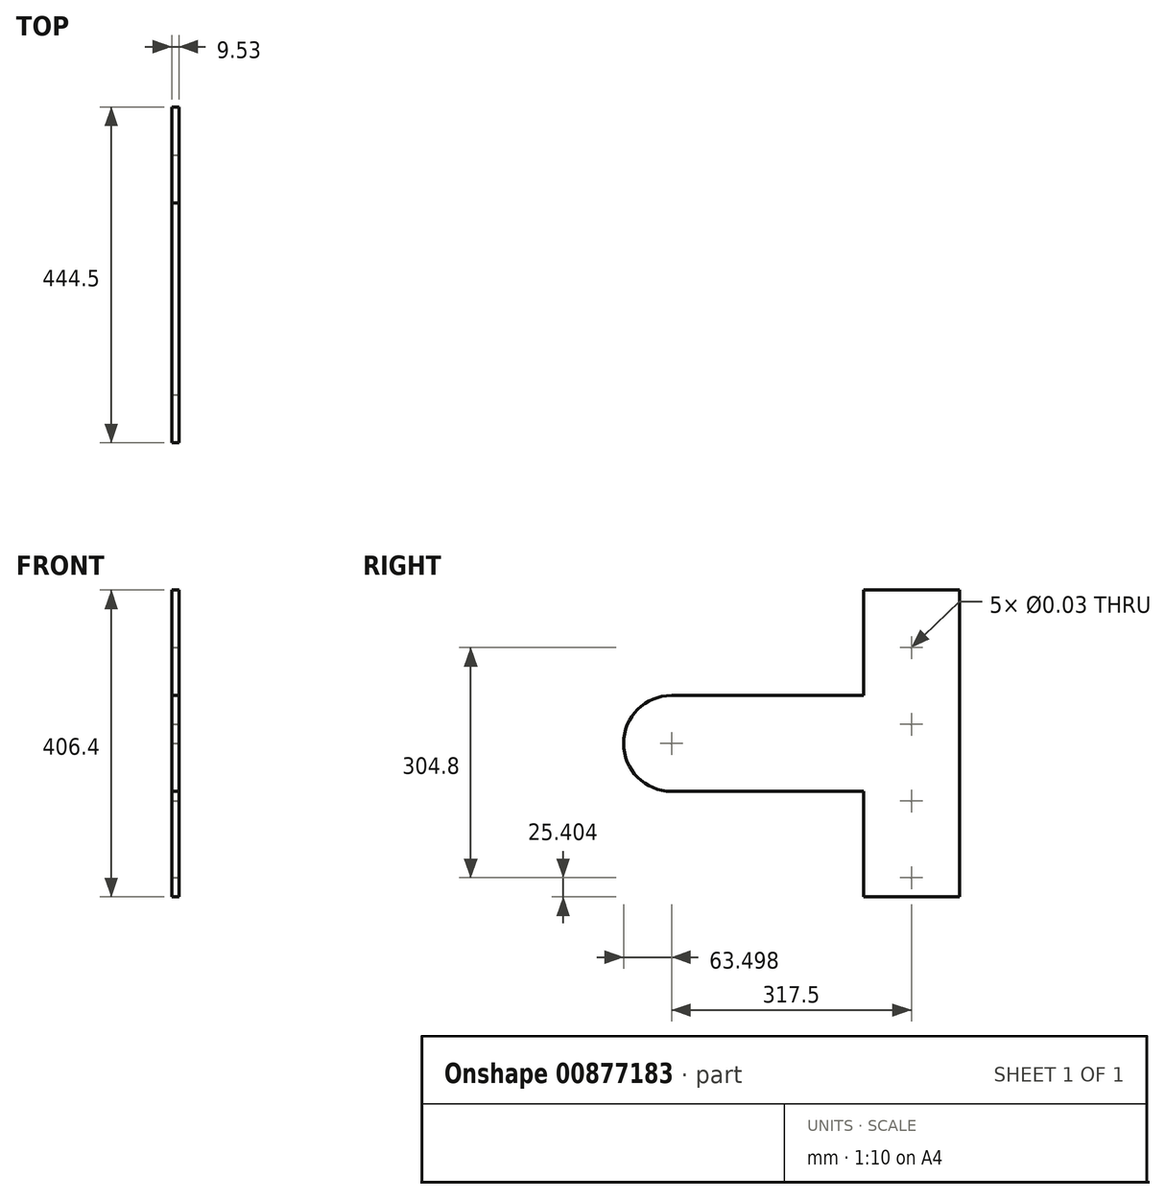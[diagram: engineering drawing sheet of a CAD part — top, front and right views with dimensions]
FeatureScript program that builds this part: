
annotation { "Feature Type Name" : "Feature", "Feature Type Description" : "" }
export const myFeature = defineFeature(function(context is Context, id is Id, definition is map)
    precondition{}
    {
        {
            var Q0;
            Q0=qCreatedBy(makeId("Right.planeOp"),FACE);
            var sketch = newSketch(context, id + "F0", { "sketchPlane" : qUnion([Q0])});
            skLineSegment(sketch, "E0.bottom", {"start": v(-37.3, -33.99) * mm, "end": v(89.7, -33.99) * mm});
            skLineSegment(sketch, "E0.top", {"start": v(-37.3, 372.41) * mm, "end": v(89.7, 372.41) * mm});
            skLineSegment(sketch, "E0.left", {"start": v(-37.3, -33.99) * mm, "end": v(-37.3, 372.41) * mm});
            skLineSegment(sketch, "E0.right", {"start": v(89.7, -33.99) * mm, "end": v(89.7, 372.41) * mm});
            skSolve(sketch);
        }
        {
            var Q0;
            Q0=makeQuery(id+"F0.imprint","IMPRINT",FACE,{"disambiguationData":[TD([[makeQuery(id+"F0.imprint","IMPRINT",EDGE,{"derivedFrom":sQuery(id+"F0.wireOp",EDGE,"E0.bottom")}),1.0]])]});
            extrude(context, id + "F1", {"entities" : qUnion([Q0]), "depth" : 9.52 * mm, "offsetDistance" : 25.4 * mm});
        }
        {
            var Q0;
            Q0=makeQuery(id+"F1.opExtrude","CAP_FACE",FACE,{"disambiguationData":[OSD([sQuery(id+"F0.wireOp",EDGE,"E0.bottom"),sQuery(id+"F0.wireOp",EDGE,"E0.top"),sQuery(id+"F0.wireOp",EDGE,"E0.left"),sQuery(id+"F0.wireOp",EDGE,"E0.right")])],"isStart":false});
            var sketch = newSketch(context, id + "F2", { "sketchPlane" : qUnion([Q0])});
            skLineSegment(sketch, "E1", {"start": v(-37.3, 169.21) * mm, "end": v(-37.3, 232.71) * mm});
            skLineSegment(sketch, "E2", {"start": v(-37.3, 232.71) * mm, "end": v(-354.8, 232.71) * mm});
            skLineSegment(sketch, "E3", {"start": v(-354.8, 232.71) * mm, "end": v(-354.8, 105.71) * mm});
            skLineSegment(sketch, "E4", {"start": v(-354.8, 105.71) * mm, "end": v(-37.3, 105.71) * mm});
            skLineSegment(sketch, "E5", {"start": v(-37.3, 105.71) * mm, "end": v(-37.3, 169.21) * mm});
            skSolve(sketch);
        }
        {
            var Q0;
            Q0=makeQuery(id+"F2.imprint","IMPRINT",FACE,{"disambiguationData":[TD([[makeQuery(id+"F2.imprint","IMPRINT",EDGE,{"derivedFrom":sQuery(id+"F2.wireOp",EDGE,"E1")}),1.0]])]});
            extrude(context, id + "F3", {"entities" : qUnion([Q0]), "operationType" : NewBodyOperationType.ADD, "oppositeDirection" : true, "depth" : 9.52 * mm, "offsetDistance" : 25.4 * mm});
        }
        {
            var Q0;
            Q0=makeQuery(id+"F3.opExtrude","SWEPT_EDGE",EDGE,{"disambiguationData":[OSD([sQuery(id+"F2.wireOp",EDGE,"E2"),sQuery(id+"F2.wireOp",EDGE,"E3")])]});
            var Q1;
            Q1=makeQuery(id+"F3.opExtrude","SWEPT_EDGE",EDGE,{"disambiguationData":[OSD([sQuery(id+"F2.wireOp",EDGE,"E3"),sQuery(id+"F2.wireOp",EDGE,"E4")])]});
            fillet(context, id + "F4", {"entities" : qUnion([Q0, Q1]), "radius" : 63.5 * mm, "tangentPropagation" : true, "allowEdgeOverflow" : false});
        }
        {
            var Q0;
            Q0=makeQuery(id+"F3.boolean.opBoolean","MERGE",FACE,{"derivedFrom":[makeQuery(id+"F1.opExtrude","CAP_FACE",FACE,{"disambiguationData":[OSD([sQuery(id+"F0.wireOp",EDGE,"E0.bottom"),sQuery(id+"F0.wireOp",EDGE,"E0.top"),sQuery(id+"F0.wireOp",EDGE,"E0.left"),sQuery(id+"F0.wireOp",EDGE,"E0.right")])],"isStart":false}),makeQuery(id+"F3.opExtrude","CAP_FACE",FACE,{"disambiguationData":[OSD([sQuery(id+"F2.wireOp",EDGE,"E1"),sQuery(id+"F2.wireOp",EDGE,"E2"),sQuery(id+"F2.wireOp",EDGE,"E3"),sQuery(id+"F2.wireOp",EDGE,"E4"),sQuery(id+"F2.wireOp",EDGE,"E5")])],"isStart":true})]});
            var sketch = newSketch(context, id + "F5", { "sketchPlane" : qUnion([Q0])});
            skCircle(sketch, "E6", {"center": v(-291.3, 169.21) * mm, "radius": 10.32 * mm});
            skSolve(sketch);
        }
        {
            var Q0;
            Q0=sQuery(id+"F5.wireOp",VERTEX,"E6.center");
            var Q1;
            Q1=makeQuery(id+"F1.opExtrude","SWEPT_BODY",BODY,{"disambiguationData":[OSD([sQuery(id+"F0.wireOp",EDGE,"E0.bottom"),sQuery(id+"F0.wireOp",EDGE,"E0.top"),sQuery(id+"F0.wireOp",EDGE,"E0.left"),sQuery(id+"F0.wireOp",EDGE,"E0.right")])]});
            hole(context, id + "F6", {"style" : HoleStyle.SIMPLE, "endStyle" : HoleEndStyle.THROUGH, "holeDiameter" : 13 / 406.4 * mm, "majorDiameter" : 6.35 * mm, "isTappedThrough" : true, "tappedDepth" : 12.7 * mm, "tapClearance" : 3, "locations" : qUnion([Q0]), "scope" : qUnion([Q1])});
        }
        {
            var Q0;
            Q0=makeQuery(id+"F3.boolean.opBoolean","MERGE",FACE,{"derivedFrom":[makeQuery(id+"F1.opExtrude","CAP_FACE",FACE,{"disambiguationData":[OSD([sQuery(id+"F0.wireOp",EDGE,"E0.bottom"),sQuery(id+"F0.wireOp",EDGE,"E0.top"),sQuery(id+"F0.wireOp",EDGE,"E0.left"),sQuery(id+"F0.wireOp",EDGE,"E0.right")])],"isStart":false}),makeQuery(id+"F3.opExtrude","CAP_FACE",FACE,{"disambiguationData":[OSD([sQuery(id+"F2.wireOp",EDGE,"E1"),sQuery(id+"F2.wireOp",EDGE,"E2"),sQuery(id+"F2.wireOp",EDGE,"E3"),sQuery(id+"F2.wireOp",EDGE,"E4"),sQuery(id+"F2.wireOp",EDGE,"E5")])],"isStart":true})]});
            var sketch = newSketch(context, id + "F7", { "sketchPlane" : qUnion([Q0])});
            skCircle(sketch, "E7", {"center": v(26.2, 296.21) * mm, "radius": 10.32 * mm});
            skCircle(sketch, "E8", {"center": v(26.2, 194.61) * mm, "radius": 10.32 * mm});
            skCircle(sketch, "E9", {"center": v(26.2, 93.01) * mm, "radius": 10.32 * mm});
            skCircle(sketch, "E10", {"center": v(26.2, -8.59) * mm, "radius": 10.32 * mm});
            skSolve(sketch);
        }
        {
            var Q0;
            Q0=sQuery(id+"F7.wireOp",VERTEX,"E7.center");
            var Q1;
            Q1=sQuery(id+"F7.wireOp",VERTEX,"E8.center");
            var Q2;
            Q2=sQuery(id+"F7.wireOp",VERTEX,"E9.center");
            var Q3;
            Q3=sQuery(id+"F7.wireOp",VERTEX,"E10.center");
            var Q4;
            Q4=makeQuery(id+"F1.opExtrude","SWEPT_BODY",BODY,{"disambiguationData":[OSD([sQuery(id+"F0.wireOp",EDGE,"E0.bottom"),sQuery(id+"F0.wireOp",EDGE,"E0.top"),sQuery(id+"F0.wireOp",EDGE,"E0.left"),sQuery(id+"F0.wireOp",EDGE,"E0.right")])]});
            hole(context, id + "F8", {"style" : HoleStyle.SIMPLE, "endStyle" : HoleEndStyle.THROUGH, "holeDiameter" : 13 / 406.4 * mm, "majorDiameter" : 6.35 * mm, "isTappedThrough" : true, "tappedDepth" : 12.7 * mm, "tapClearance" : 3, "locations" : qUnion([Q0, Q1, Q2, Q3]), "scope" : qUnion([Q4])});
        }
    });
